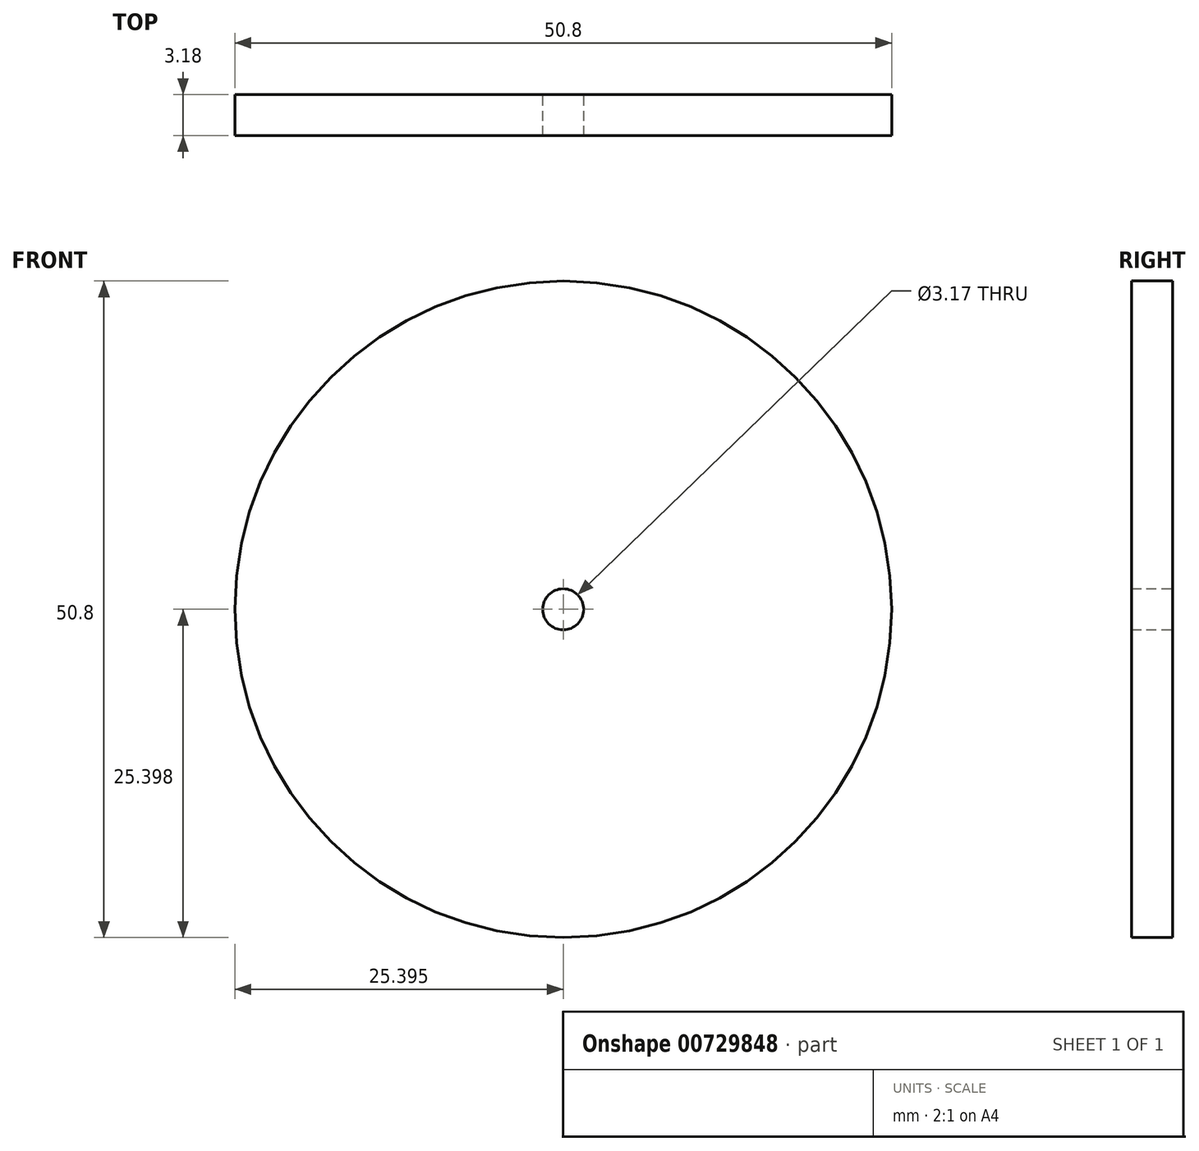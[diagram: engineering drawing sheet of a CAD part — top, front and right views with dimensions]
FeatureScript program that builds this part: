
annotation { "Feature Type Name" : "Feature", "Feature Type Description" : "" }
export const myFeature = defineFeature(function(context is Context, id is Id, definition is map)
    precondition{}
    {
        {
            var Q0;
            Q0=qCreatedBy(makeId("Front.planeOp"),FACE);
            var sketch = newSketch(context, id + "F0", { "sketchPlane" : qUnion([Q0])});
            skCircle(sketch, "E0", {"center": v(2.79, -1.8) * mm, "radius": 25.4 * mm});
            skCircle(sketch, "E1", {"center": v(2.79, -1.8) * mm, "radius": 1.59 * mm});
            skSolve(sketch);
        }
        {
            var Q0;
            Q0=makeQuery(id+"F0.imprint","IMPRINT",FACE,{"disambiguationData":[TD([[makeQuery(id+"F0.imprint","IMPRINT",EDGE,{"derivedFrom":sQuery(id+"F0.wireOp",EDGE,"E0")}),1.0]])]});
            extrude(context, id + "F1", {"entities" : qUnion([Q0]), "depth" : 3.17 * mm, "offsetDistance" : 25.4 * mm});
        }
    });
